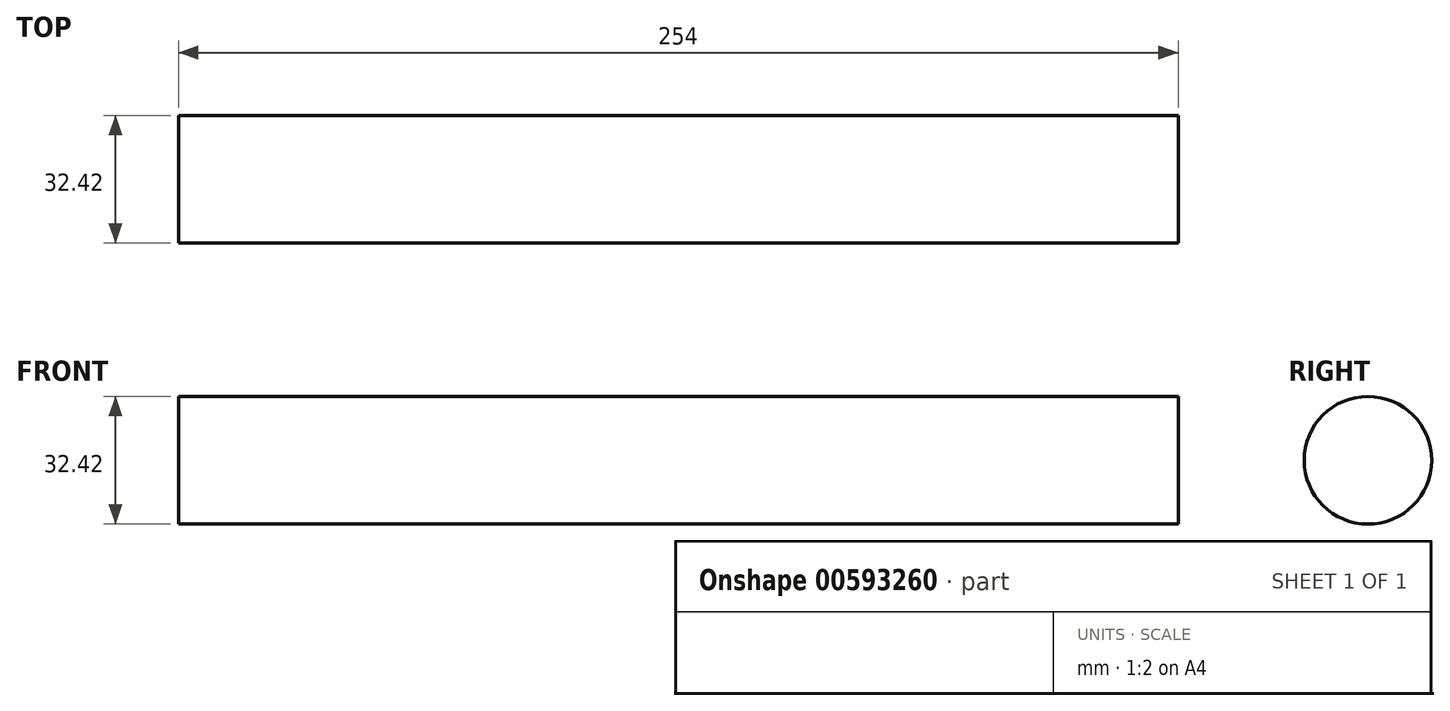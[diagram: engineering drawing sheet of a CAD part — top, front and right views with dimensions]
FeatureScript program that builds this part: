
annotation { "Feature Type Name" : "Feature", "Feature Type Description" : "" }
export const myFeature = defineFeature(function(context is Context, id is Id, definition is map)
    precondition{}
    {
        {
            var Q0;
            Q0=qCreatedBy(makeId("Right.planeOp"),FACE);
            var sketch = newSketch(context, id + "F0", { "sketchPlane" : qUnion([Q0])});
            skCircle(sketch, "E0", {"center": v(-56.87, 20.12) * mm, "radius": 16.21 * mm});
            skSolve(sketch);
        }
        {
            var Q0;
            Q0 = qSketchRegion(id + "F0", true);
            extrude(context, id + "F1", {"entities" : qUnion([Q0]), "depth" : 254 * mm, "offsetDistance" : 25.4 * mm});
        }
    });
